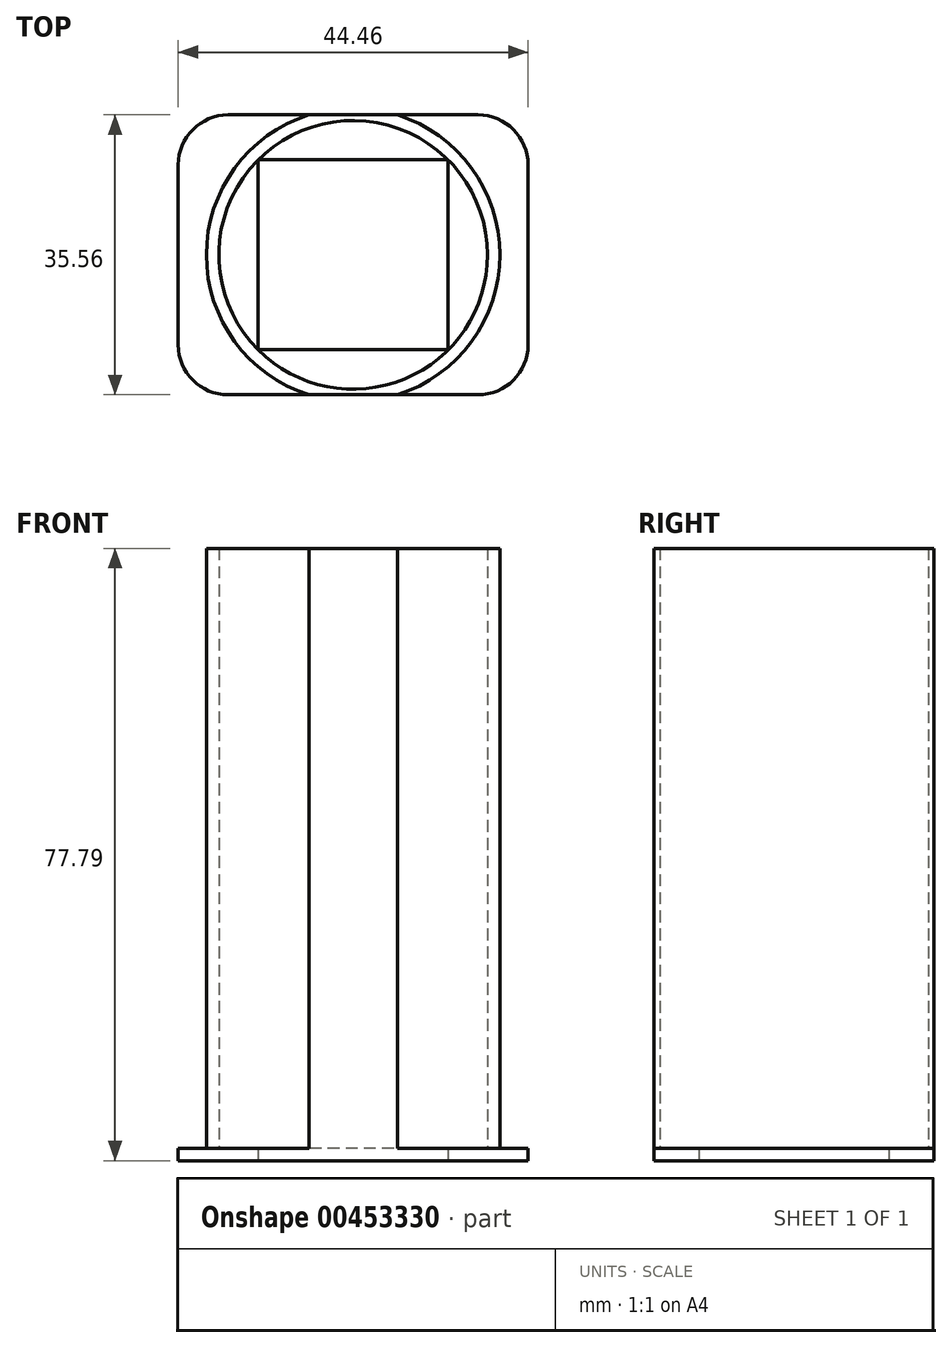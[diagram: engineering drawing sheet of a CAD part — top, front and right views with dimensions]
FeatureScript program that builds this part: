
annotation { "Feature Type Name" : "Feature", "Feature Type Description" : "" }
export const myFeature = defineFeature(function(context is Context, id is Id, definition is map)
    precondition{}
    {
        {
            var Q0;
            Q0=qCreatedBy(makeId("Top.planeOp"),FACE);
            var sketch = newSketch(context, id + "F0", { "sketchPlane" : qUnion([Q0])});
            skLineSegment(sketch, "E0.bottom", {"start": v(12.06, 12.07) * mm, "end": v(-12.07, 12.06) * mm});
            skLineSegment(sketch, "E0.top", {"start": v(12.07, -12.07) * mm, "end": v(-12.06, -12.07) * mm});
            skLineSegment(sketch, "E0.left", {"start": v(12.07, 12.07) * mm, "end": v(12.07, -12.07) * mm});
            skLineSegment(sketch, "E0.right", {"start": v(-12.07, 12.06) * mm, "end": v(-12.07, -12.07) * mm});
            skPoint(sketch, "E0.middle", {"position": v(0, 0) * mm});
            skLineSegment(sketch, "E1.bottom", {"start": v(22.23, -17.78) * mm, "end": v(-22.22, -17.78) * mm});
            skLineSegment(sketch, "E1.top", {"start": v(22.22, 17.78) * mm, "end": v(-22.23, 17.78) * mm});
            skLineSegment(sketch, "E1.left", {"start": v(22.23, -17.78) * mm, "end": v(22.22, 17.78) * mm});
            skLineSegment(sketch, "E1.right", {"start": v(-22.22, -17.78) * mm, "end": v(-22.23, 17.78) * mm});
            skLineSegment(sketch, "E2.bottom", {"start": v(-22.22, -17.78) * mm, "end": v(22.23, -17.78) * mm});
            skLineSegment(sketch, "E2.top", {"start": v(-22.22, -36.83) * mm, "end": v(22.23, -36.83) * mm});
            skLineSegment(sketch, "E2.left", {"start": v(-22.22, -17.78) * mm, "end": v(-22.22, -36.83) * mm});
            skLineSegment(sketch, "E2.right", {"start": v(22.23, -17.78) * mm, "end": v(22.23, -36.83) * mm});
            skLineSegment(sketch, "E3.bottom", {"start": v(0, 17.78) * mm, "end": v(12.7, 17.78) * mm});
            skLineSegment(sketch, "E3.top", {"start": v(0, 30.48) * mm, "end": v(12.7, 30.48) * mm});
            skLineSegment(sketch, "E3.left", {"start": v(0, 17.78) * mm, "end": v(0, 30.48) * mm});
            skLineSegment(sketch, "E3.right", {"start": v(12.7, 17.78) * mm, "end": v(12.7, 30.48) * mm});
            skLineSegment(sketch, "E4.bottom", {"start": v(0, 17.78) * mm, "end": v(-12.7, 17.78) * mm});
            skLineSegment(sketch, "E4.top", {"start": v(0, 30.48) * mm, "end": v(-12.7, 30.48) * mm});
            skLineSegment(sketch, "E4.right", {"start": v(-12.7, 17.78) * mm, "end": v(-12.7, 30.48) * mm});
            skCircle(sketch, "E5", {"center": v(0, 24.13) * mm, "radius": 1.02 * mm});
            skCircle(sketch, "E6", {"center": v(0, -24.13) * mm, "radius": 1.02 * mm});
            skLineSegment(sketch, "E7.bottom", {"start": v(-22.22, -17.78) * mm, "end": v(22.23, -17.78) * mm, "construction": true});
            skLineSegment(sketch, "E7.top", {"start": v(-22.22, -30.48) * mm, "end": v(22.23, -30.48) * mm, "construction": true});
            skLineSegment(sketch, "E7.left", {"start": v(-22.22, -17.78) * mm, "end": v(-22.22, -30.48) * mm, "construction": true});
            skLineSegment(sketch, "E7.right", {"start": v(22.23, -17.78) * mm, "end": v(22.23, -30.48) * mm, "construction": true});
            skLineSegment(sketch, "E8", {"start": v(0, -17.78) * mm, "end": v(0, -30.48) * mm, "construction": true});
            skSolve(sketch);
        }
        {
            var Q0;
            Q0=makeQuery(id+"F0.imprint","IMPRINT",FACE,{"disambiguationData":[TD([[makeQuery(id+"F0.imprint","IMPRINT",EDGE,{"derivedFrom":sQuery(id+"F0.wireOp",EDGE,"E3.bottom")}),1.0]])]});
            var Q1;
            Q1=makeQuery(id+"F0.imprint","IMPRINT",FACE,{"disambiguationData":[TD([[makeQuery(id+"F0.imprint","IMPRINT",EDGE,{"derivedFrom":sQuery(id+"F0.wireOp",EDGE,"E4.bottom")}),-1.0]])]});
            var Q2;
            Q2=makeQuery(id+"F0.imprint","IMPRINT",FACE,{"disambiguationData":[TD([[makeQuery(id+"F0.imprint","IMPRINT",EDGE,{"derivedFrom":sQuery(id+"F0.wireOp",EDGE,"E0.bottom")}),-1.0]])]});
            var Q3;
            Q3=makeQuery(id+"F0.imprint","IMPRINT",FACE,{"disambiguationData":[TD([[makeQuery(id+"F0.imprint","IMPRINT",EDGE,{"derivedFrom":sQuery(id+"F0.wireOp",EDGE,"E2.bottom")}),-1.0]])]});
            extrude(context, id + "F1", {"entities" : qUnion([Q0, Q1, Q2, Q3]), "depth" : 1.59 * mm});
        }
        {
            var Q0;
            Q0=makeQuery(id+"F1.opExtrude","SWEPT_EDGE",EDGE,{"disambiguationData":[OSD([sQuery(id+"F0.wireOp",EDGE,"E4.top"),sQuery(id+"F0.wireOp",EDGE,"E4.right")])]});
            var Q1;
            Q1=makeQuery(id+"F1.opExtrude","SWEPT_EDGE",EDGE,{"disambiguationData":[OSD([sQuery(id+"F0.wireOp",EDGE,"E1.top"),sQuery(id+"F0.wireOp",EDGE,"E1.right")])]});
            var Q2;
            Q2=makeQuery(id+"F1.opExtrude","SWEPT_EDGE",EDGE,{"disambiguationData":[OSD([sQuery(id+"F0.wireOp",EDGE,"E3.top"),sQuery(id+"F0.wireOp",EDGE,"E3.right")])]});
            var Q3;
            Q3=makeQuery(id+"F1.opExtrude","SWEPT_EDGE",EDGE,{"disambiguationData":[OSD([sQuery(id+"F0.wireOp",EDGE,"E1.top"),sQuery(id+"F0.wireOp",EDGE,"E1.left")])]});
            var Q4;
            Q4=makeQuery(id+"F1.opExtrude","SWEPT_EDGE",EDGE,{"disambiguationData":[OSD([sQuery(id+"F0.wireOp",EDGE,"E2.top"),sQuery(id+"F0.wireOp",EDGE,"E2.right")])]});
            var Q5;
            Q5=makeQuery(id+"F1.opExtrude","SWEPT_EDGE",EDGE,{"disambiguationData":[OSD([sQuery(id+"F0.wireOp",EDGE,"E2.top"),sQuery(id+"F0.wireOp",EDGE,"E2.left")])]});
            fillet(context, id + "F2", {"entities" : qUnion([Q0, Q1, Q2, Q3, Q4, Q5]), "radius" : 6.35 * mm, "tangentPropagation" : true, "allowEdgeOverflow" : false});
        }
        {
            var Q0;
            Q0=makeQuery(id+"F1.opExtrude","CAP_FACE",FACE,{"disambiguationData":[OSD([sQuery(id+"F0.wireOp",EDGE,"E0.bottom"),sQuery(id+"F0.wireOp",EDGE,"E0.top"),sQuery(id+"F0.wireOp",EDGE,"E0.left"),sQuery(id+"F0.wireOp",EDGE,"E0.right"),sQuery(id+"F0.wireOp",EDGE,"E1.top"),sQuery(id+"F0.wireOp",EDGE,"E1.left"),sQuery(id+"F0.wireOp",EDGE,"E1.right"),sQuery(id+"F0.wireOp",EDGE,"E2.top"),sQuery(id+"F0.wireOp",EDGE,"E2.left"),sQuery(id+"F0.wireOp",EDGE,"E2.right"),sQuery(id+"F0.wireOp",EDGE,"E3.top"),sQuery(id+"F0.wireOp",EDGE,"E3.right"),sQuery(id+"F0.wireOp",EDGE,"E4.top"),sQuery(id+"F0.wireOp",EDGE,"E4.right"),sQuery(id+"F0.wireOp",EDGE,"E5"),sQuery(id+"F0.wireOp",EDGE,"E6")])],"isStart":false});
            var sketch = newSketch(context, id + "F3", { "sketchPlane" : qUnion([Q0])});
            skCircle(sketch, "E9", {"center": v(0, 0) * mm, "radius": 18.65 * mm});
            skCircle(sketch, "E10", {"center": v(0, 0) * mm, "radius": 17.06 * mm});
            skLineSegment(sketch, "E11", {"start": v(17.06, 0) * mm, "end": v(18.65, 0) * mm, "construction": true});
            skSolve(sketch);
        }
        {
            var Q0;
            Q0=makeQuery(id+"F3.imprint","IMPRINT",FACE,{"disambiguationData":[TD([[makeQuery(id+"F3.imprint","IMPRINT",EDGE,{"derivedFrom":sQuery(id+"F3.wireOp",EDGE,"E10")}),-1.0]])]});
            extrude(context, id + "F4", {"entities" : qUnion([Q0]), "operationType" : NewBodyOperationType.ADD, "depth" : 76.2 * mm});
        }
    });
